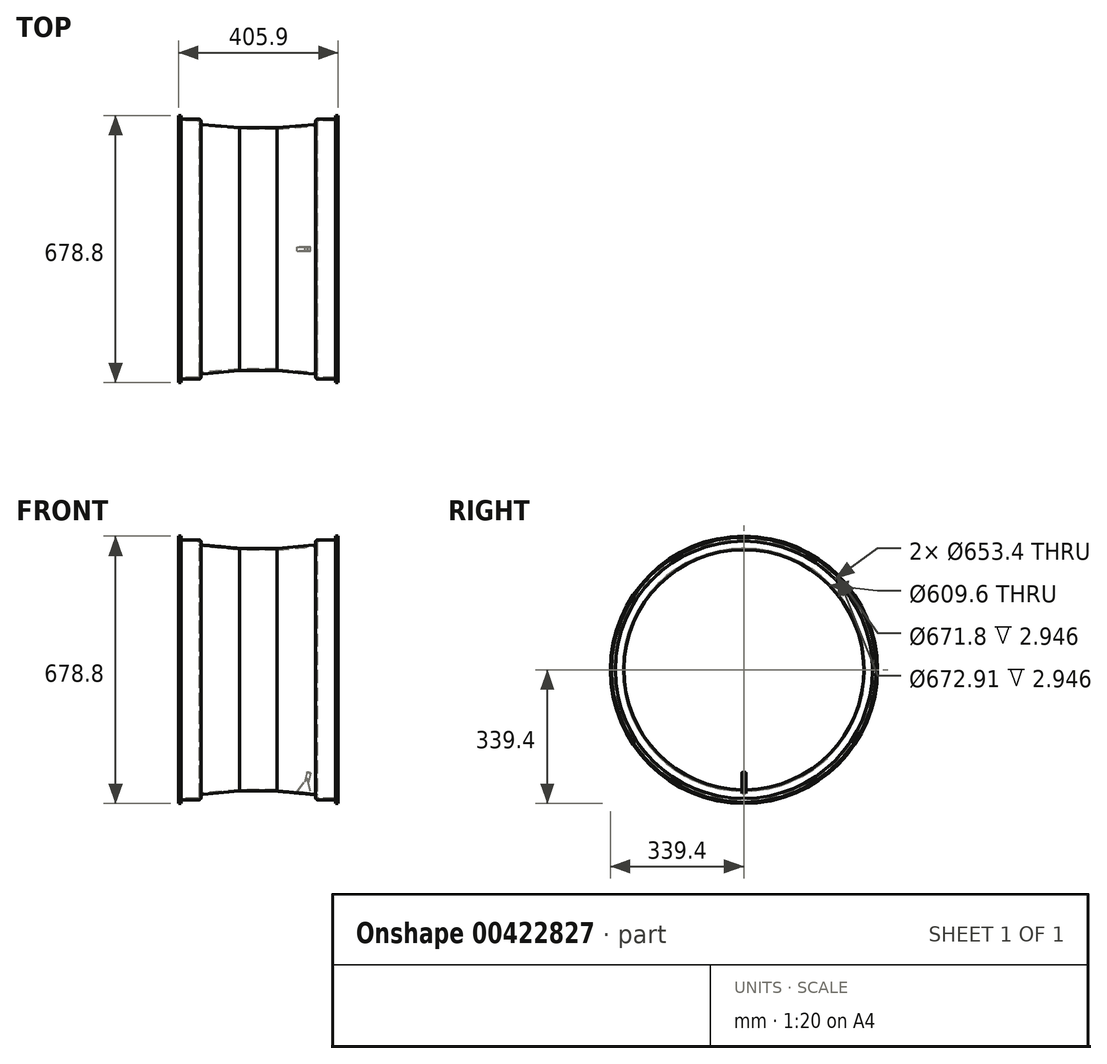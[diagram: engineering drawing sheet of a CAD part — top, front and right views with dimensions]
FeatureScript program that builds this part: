
annotation { "Feature Type Name" : "Feature", "Feature Type Description" : "" }
export const myFeature = defineFeature(function(context is Context, id is Id, definition is map)
    precondition{}
    {
        {
            var Q0;
            Q0=qCreatedBy(makeId("Front.planeOp"),FACE);
            var sketch = newSketch(context, id + "F0", { "sketchPlane" : qUnion([Q0])});
            skLineSegment(sketch, "E0", {"start": v(-127, 339.4) * mm, "end": v(-127, 326.7) * mm});
            skLineSegment(sketch, "E1", {"start": v(-127, 326.7) * mm, "end": v(-76.2, 326.7) * mm});
            skLineSegment(sketch, "E2", {"start": v(-76.2, 326.7) * mm, "end": v(-76.2, 314) * mm});
            skLineSegment(sketch, "E3", {"start": v(-76.2, 314) * mm, "end": v(25.4, 304.8) * mm});
            skLineSegment(sketch, "E4", {"start": v(25.4, 304.8) * mm, "end": v(120.6, 304.8) * mm});
            skLineSegment(sketch, "E5", {"start": v(120.6, 304.8) * mm, "end": v(222.2, 314) * mm});
            skLineSegment(sketch, "E6", {"start": v(222.2, 314) * mm, "end": v(222.2, 326.7) * mm});
            skLineSegment(sketch, "E7", {"start": v(222.2, 326.7) * mm, "end": v(273, 326.7) * mm});
            skLineSegment(sketch, "E8", {"start": v(273, 326.7) * mm, "end": v(273, 339.4) * mm});
            skLineSegment(sketch, "E9.0", {"start": v(269.5, 330.2) * mm, "end": v(269.5, 339.4) * mm});
            skLineSegment(sketch, "E9.1", {"start": v(218.7, 330.2) * mm, "end": v(269.5, 330.2) * mm});
            skLineSegment(sketch, "E9.2", {"start": v(218.7, 317.2) * mm, "end": v(218.7, 330.2) * mm});
            skLineSegment(sketch, "E9.3", {"start": v(120.44, 308.3) * mm, "end": v(218.7, 317.2) * mm});
            skLineSegment(sketch, "E9.4", {"start": v(25.56, 308.3) * mm, "end": v(120.44, 308.3) * mm});
            skLineSegment(sketch, "E9.5", {"start": v(-123.5, 339.4) * mm, "end": v(-123.5, 330.2) * mm});
            skLineSegment(sketch, "E9.6", {"start": v(-123.5, 330.2) * mm, "end": v(-72.7, 330.2) * mm});
            skLineSegment(sketch, "E9.7", {"start": v(-72.7, 330.2) * mm, "end": v(-72.7, 317.2) * mm});
            skLineSegment(sketch, "E9.8", {"start": v(-72.7, 317.2) * mm, "end": v(25.56, 308.3) * mm});
            skLineSegment(sketch, "E10", {"start": v(-127, 339.4) * mm, "end": v(-123.5, 339.4) * mm});
            skLineSegment(sketch, "E11", {"start": v(269.5, 339.4) * mm, "end": v(273, 339.4) * mm});
            skSolve(sketch);
        }
        {
            var Q0;
            Q0=qCreatedBy(makeId("Front.planeOp"),FACE);
            var sketch = newSketch(context, id + "F1", { "sketchPlane" : qUnion([Q0])});
            skPoint(sketch, "E12.0", {"position": v(-127, 339.4) * mm});
            skLineSegment(sketch, "E13.bottom", {"start": v(-127, 339.4) * mm, "end": v(-129.95, 339.4) * mm});
            skLineSegment(sketch, "E13.top", {"start": v(-127, 335.9) * mm, "end": v(-129.95, 335.9) * mm});
            skLineSegment(sketch, "E13.left", {"start": v(-127, 339.4) * mm, "end": v(-127, 335.9) * mm});
            skLineSegment(sketch, "E13.right", {"start": v(-129.95, 339.4) * mm, "end": v(-129.95, 335.9) * mm});
            skPoint(sketch, "E14.0", {"position": v(273, 339.4) * mm});
            skLineSegment(sketch, "E15.bottom", {"start": v(273, 339.4) * mm, "end": v(275.95, 339.4) * mm});
            skLineSegment(sketch, "E15.top", {"start": v(273, 336.45) * mm, "end": v(275.95, 336.45) * mm});
            skLineSegment(sketch, "E15.left", {"start": v(273, 339.4) * mm, "end": v(273, 336.45) * mm});
            skLineSegment(sketch, "E15.right", {"start": v(275.95, 339.4) * mm, "end": v(275.95, 336.45) * mm});
            skSolve(sketch);
        }
        {
            var Q0;
            Q0=qCreatedBy(makeId("Front.planeOp"),FACE);
            var sketch = newSketch(context, id + "F2", { "sketchPlane" : qUnion([Q0])});
            skLineSegment(sketch, "E16", {"start": v(0, 0) * mm, "end": v(393.24, 0) * mm});
            skSolve(sketch);
        }
        {
            var Q0;
            Q0=makeQuery(id+"F0.imprint","IMPRINT",FACE,{"disambiguationData":[TD([[makeQuery(id+"F0.imprint","IMPRINT",EDGE,{"derivedFrom":sQuery(id+"F0.wireOp",EDGE,"E0")}),1.0]])]});
            var Q1;
            Q1=sQuery(id+"F2.wireOp",EDGE,"E16");
            revolve(context, id + "F3", {"entities" : qUnion([Q0]), "axis" : qUnion([Q1]), "revolveType" : RevolveType.FULL});
        }
        {
            var Q0;
            Q0 = qSketchRegion(id + "F1", true);
            var Q1;
            Q1=sQuery(id+"F2.wireOp",EDGE,"E16");
            revolve(context, id + "F4", {"operationType" : NewBodyOperationType.ADD, "entities" : qUnion([Q0]), "axis" : qUnion([Q1]), "revolveType" : RevolveType.FULL});
        }
        {
            var Q0;
            Q0=qCreatedBy(makeId("Front.planeOp"),FACE);
            var sketch = newSketch(context, id + "F5", { "sketchPlane" : qUnion([Q0])});
            skLineSegment(sketch, "E17", {"start": v(171.97, -310.05) * mm, "end": v(189.97, -285.45) * mm});
            skLineSegment(sketch, "E18", {"start": v(189.97, -285.45) * mm, "end": v(196.56, -259.98) * mm});
            skLineSegment(sketch, "E19", {"start": v(196.56, -259.98) * mm, "end": v(206.24, -262.48) * mm});
            skLineSegment(sketch, "E20", {"start": v(206.24, -262.48) * mm, "end": v(199.52, -288.5) * mm});
            skLineSegment(sketch, "E21", {"start": v(199.52, -288.5) * mm, "end": v(206.23, -314.44) * mm});
            skLineSegment(sketch, "E22", {"start": v(206.23, -314.44) * mm, "end": v(171.97, -310.05) * mm});
            skSolve(sketch);
        }
        {
            var Q0;
            Q0=makeQuery(id+"F5.imprint","IMPRINT",FACE,{"disambiguationData":[TD([[makeQuery(id+"F5.imprint","IMPRINT",EDGE,{"derivedFrom":sQuery(id+"F5.wireOp",EDGE,"E17")}),-1.0]])]});
            extrude(context, id + "F6", {"entities" : qUnion([Q0]), "endBound" : BoundingType.SYMMETRIC, "depth" : 10 * mm});
        }
        {
            var Q0;
            Q0=makeQuery(id+"F6.opExtrude","CAP_EDGE",EDGE,{"disambiguationData":[OSD([sQuery(id+"F5.wireOp",EDGE,"E18")])],"isStart":false});
            var Q1;
            Q1=makeQuery(id+"F6.opExtrude","CAP_EDGE",EDGE,{"disambiguationData":[OSD([sQuery(id+"F5.wireOp",EDGE,"E20")])],"isStart":false});
            var Q2;
            Q2=makeQuery(id+"F6.opExtrude","CAP_EDGE",EDGE,{"disambiguationData":[OSD([sQuery(id+"F5.wireOp",EDGE,"E20")])],"isStart":true});
            var Q3;
            Q3=makeQuery(id+"F6.opExtrude","CAP_EDGE",EDGE,{"disambiguationData":[OSD([sQuery(id+"F5.wireOp",EDGE,"E18")])],"isStart":true});
            fillet(context, id + "F7", {"entities" : qUnion([Q0, Q1, Q2, Q3]), "radius" : 5 * mm, "tangentPropagation" : true, "allowEdgeOverflow" : false});
        }
        {
            var Q0;
            Q0=makeQuery(id+"F3.opRevolve","SWEPT_EDGE",EDGE,{"disambiguationData":[OSD([sQuery(id+"F0.wireOp",EDGE,"E5"),sQuery(id+"F0.wireOp",EDGE,"E6")])]});
            var Q1;
            Q1=makeQuery(id+"F3.opRevolve","SWEPT_EDGE",EDGE,{"disambiguationData":[OSD([sQuery(id+"F0.wireOp",EDGE,"E2"),sQuery(id+"F0.wireOp",EDGE,"E3")])]});
            fillet(context, id + "F8", {"entities" : qUnion([Q0, Q1]), "radius" : 5.08 * mm, "tangentPropagation" : true, "allowEdgeOverflow" : false});
        }
        {
            var Q0;
            Q0=makeQuery(id+"F3.opRevolve","SWEPT_EDGE",EDGE,{"disambiguationData":[OSD([sQuery(id+"F0.wireOp",EDGE,"E6"),sQuery(id+"F0.wireOp",EDGE,"E7")])]});
            var Q1;
            Q1=makeQuery(id+"F3.opRevolve","SWEPT_EDGE",EDGE,{"disambiguationData":[OSD([sQuery(id+"F0.wireOp",EDGE,"E1"),sQuery(id+"F0.wireOp",EDGE,"E2")])]});
            fillet(context, id + "F9", {"entities" : qUnion([Q0, Q1]), "radius" : 5.08 * mm, "tangentPropagation" : true, "allowEdgeOverflow" : false});
        }
        {
            var Q0;
            Q0=makeQuery(id+"F3.opRevolve","SWEPT_EDGE",EDGE,{"disambiguationData":[OSD([sQuery(id+"F0.wireOp",EDGE,"E9.6"),sQuery(id+"F0.wireOp",EDGE,"E9.7")])]});
            var Q1;
            Q1=makeQuery(id+"F3.opRevolve","SWEPT_EDGE",EDGE,{"disambiguationData":[OSD([sQuery(id+"F0.wireOp",EDGE,"E9.1"),sQuery(id+"F0.wireOp",EDGE,"E9.2")])]});
            fillet(context, id + "F10", {"entities" : qUnion([Q0, Q1]), "radius" : 5.08 * mm, "tangentPropagation" : true, "allowEdgeOverflow" : false});
        }
        {
            var Q0;
            Q0=makeQuery(id+"F3.opRevolve","SWEPT_EDGE",EDGE,{"disambiguationData":[OSD([sQuery(id+"F0.wireOp",EDGE,"E7"),sQuery(id+"F0.wireOp",EDGE,"E8")])]});
            var Q1;
            Q1=makeQuery(id+"F3.opRevolve","SWEPT_EDGE",EDGE,{"disambiguationData":[OSD([sQuery(id+"F0.wireOp",EDGE,"E0"),sQuery(id+"F0.wireOp",EDGE,"E1")])]});
            fillet(context, id + "F11", {"entities" : qUnion([Q0, Q1]), "radius" : 5.08 * mm, "tangentPropagation" : true, "allowEdgeOverflow" : false});
        }
        {
            var Q0;
            Q0=makeQuery(id+"F3.opRevolve","SWEPT_EDGE",EDGE,{"disambiguationData":[OSD([sQuery(id+"F0.wireOp",EDGE,"E9.0"),sQuery(id+"F0.wireOp",EDGE,"E9.1")])]});
            var Q1;
            Q1=makeQuery(id+"F3.opRevolve","SWEPT_EDGE",EDGE,{"disambiguationData":[OSD([sQuery(id+"F0.wireOp",EDGE,"E9.5"),sQuery(id+"F0.wireOp",EDGE,"E9.6")])]});
            fillet(context, id + "F12", {"entities" : qUnion([Q0, Q1]), "radius" : 5.08 * mm, "tangentPropagation" : true, "allowEdgeOverflow" : false});
        }
        {
            var Q0;
            Q0=makeQuery(id+"F3.opRevolve","SWEPT_EDGE",EDGE,{"disambiguationData":[OSD([sQuery(id+"F0.wireOp",EDGE,"E9.7"),sQuery(id+"F0.wireOp",EDGE,"E9.8")])]});
            var Q1;
            Q1=makeQuery(id+"F3.opRevolve","SWEPT_EDGE",EDGE,{"disambiguationData":[OSD([sQuery(id+"F0.wireOp",EDGE,"E9.2"),sQuery(id+"F0.wireOp",EDGE,"E9.3")])]});
            fillet(context, id + "F13", {"entities" : qUnion([Q0, Q1]), "radius" : 5.08 * mm, "tangentPropagation" : true, "allowEdgeOverflow" : false});
        }
    });
